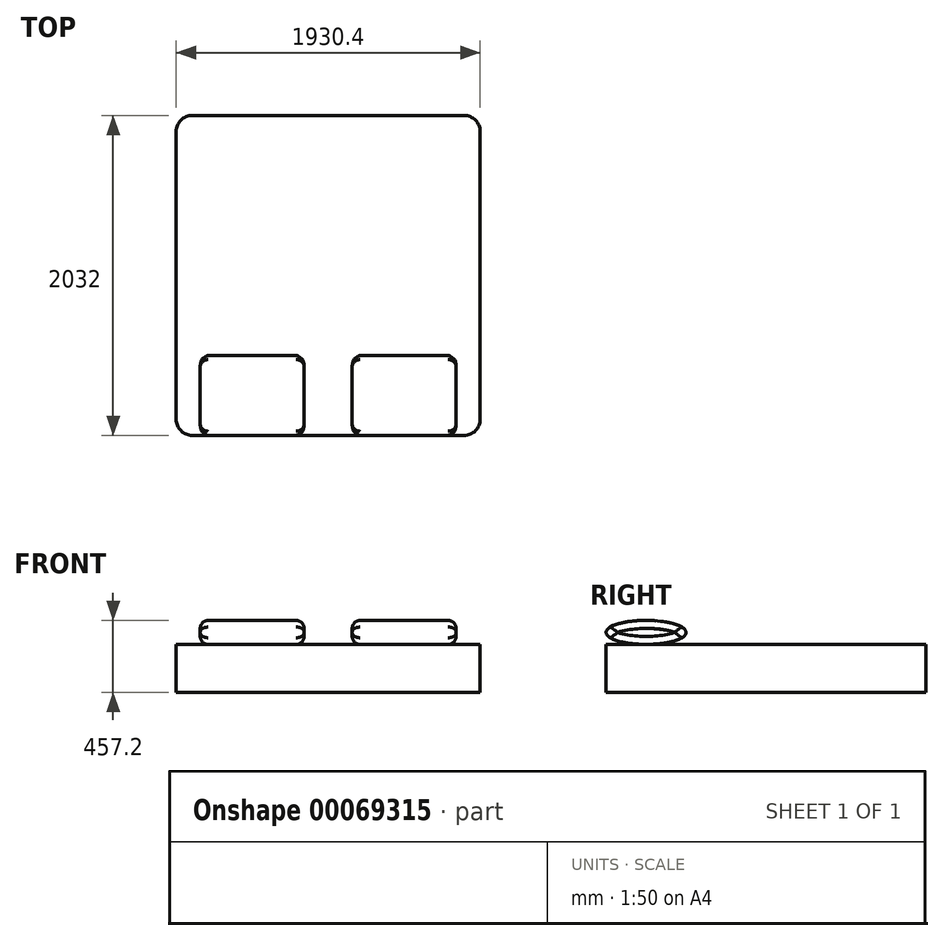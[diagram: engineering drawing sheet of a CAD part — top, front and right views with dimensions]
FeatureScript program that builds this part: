
annotation { "Feature Type Name" : "Feature", "Feature Type Description" : "" }
export const myFeature = defineFeature(function(context is Context, id is Id, definition is map)
    precondition{}
    {
        {
            var Q0;
            Q0=qCreatedBy(makeId("Top.planeOp"),FACE);
            var sketch = newSketch(context, id + "F0", { "sketchPlane" : qUnion([Q0])});
            skLineSegment(sketch, "E0.rect.bottom", {"start": v(-965.2, -1016) * mm, "end": v(965.2, -1016) * mm});
            skLineSegment(sketch, "E0.rect.top", {"start": v(-965.2, 1016) * mm, "end": v(965.2, 1016) * mm});
            skLineSegment(sketch, "E0.rect.left", {"start": v(-965.2, -1016) * mm, "end": v(-965.2, 1016) * mm});
            skLineSegment(sketch, "E0.rect.right", {"start": v(965.2, -1016) * mm, "end": v(965.2, 1016) * mm});
            skPoint(sketch, "E0.rect.middle", {"position": v(0, 0) * mm});
            skSolve(sketch);
        }
        {
            var Q0;
            Q0 = qSketchRegion(id + "F0", true);
            extrude(context, id + "F1", {"entities" : qUnion([Q0]), "depth" : 304.8 * mm});
        }
        {
            var Q0;
            Q0=makeQuery(id+"F1.opExtrude","SWEPT_EDGE",EDGE,{"disambiguationData":[OSD([sQuery(id+"F0.wireOp",EDGE,"E0.rect.top"),sQuery(id+"F0.wireOp",EDGE,"E0.rect.left")])]});
            var Q1;
            Q1=makeQuery(id+"F1.opExtrude","SWEPT_EDGE",EDGE,{"disambiguationData":[OSD([sQuery(id+"F0.wireOp",EDGE,"E0.rect.top"),sQuery(id+"F0.wireOp",EDGE,"E0.rect.right")])]});
            var Q2;
            Q2=makeQuery(id+"F1.opExtrude","SWEPT_EDGE",EDGE,{"disambiguationData":[OSD([sQuery(id+"F0.wireOp",EDGE,"E0.rect.bottom"),sQuery(id+"F0.wireOp",EDGE,"E0.rect.left")])]});
            var Q3;
            Q3=makeQuery(id+"F1.opExtrude","SWEPT_EDGE",EDGE,{"disambiguationData":[OSD([sQuery(id+"F0.wireOp",EDGE,"E0.rect.bottom"),sQuery(id+"F0.wireOp",EDGE,"E0.rect.right")])]});
            fillet(context, id + "F2", {"entities" : qUnion([Q0, Q1, Q2, Q3]), "radius" : 101.6 * mm, "tangentPropagation" : true, "allowEdgeOverflow" : false});
        }
        {
            var Q0;
            Q0=qCreatedBy(makeId("Right.planeOp"),FACE);
            cPlane(context, id + "F3", {"entities" : qUnion([Q0]), "cplaneType" : CPlaneType.OFFSET, "offset" : 482.6 * mm, "width" : 152.4 * mm, "height" : 152.4 * mm});
        }
        {
            var Q0;
            Q0=qCreatedBy(id+"F3.planeOp",FACE);
            var sketch = newSketch(context, id + "F4", { "sketchPlane" : qUnion([Q0])});
            skEllipse(sketch, "E1", {"center": v(-762, 381) * mm, "majorRadius": 254 * mm, "minorRadius": 76.2 * mm, "majorAxis": v(1, 0)});
            skLineSegment(sketch, "E2", {"start": v(-762, 457.2) * mm, "end": v(-762, 304.8) * mm, "construction": true});
            skSolve(sketch);
        }
        {
            var Q0;
            Q0 = qSketchRegion(id + "F4", true);
            extrude(context, id + "F5", {"entities" : qUnion([Q0]), "operationType" : NewBodyOperationType.ADD, "endBound" : BoundingType.SYMMETRIC, "depth" : 660.4 * mm});
        }
        {
            var Q0;
            Q0=makeQuery(id+"F5.opExtrude","SWEPT_BODY",BODY,{"disambiguationData":[OSD([sQuery(id+"F4.wireOp",EDGE,"E1")])]});
            var Q1;
            Q1=qCreatedBy(makeId("Right.planeOp"),FACE);
            mirror(context, id + "F6", {"operationType" : NewBodyOperationType.ADD, "entities" : qUnion([Q0]), "mirrorPlane" : qUnion([Q1])});
        }
        {
            var Q0;
            Q0=makeQuery(id+"F6.opPattern","COPY",EDGE,{"derivedFrom":makeQuery(id+"F5.opExtrude","CAP_EDGE",EDGE,{"disambiguationData":[OSD([sQuery(id+"F4.wireOp",EDGE,"E1")])],"isStart":true}),"instanceName":"1"});
            fillet(context, id + "F7", {"entities" : qUnion([Q0]), "radius" : 50.8 * mm, "tangentPropagation" : true, "allowEdgeOverflow" : false});
        }
        {
            var Q0;
            Q0=makeQuery(id+"F6.opPattern","COPY",EDGE,{"derivedFrom":makeQuery(id+"F5.opExtrude","CAP_EDGE",EDGE,{"disambiguationData":[OSD([sQuery(id+"F4.wireOp",EDGE,"E1")])],"isStart":false}),"instanceName":"1"});
            var Q1;
            Q1=makeQuery(id+"F5.opExtrude","CAP_EDGE",EDGE,{"disambiguationData":[OSD([sQuery(id+"F4.wireOp",EDGE,"E1")])],"isStart":true});
            var Q2;
            Q2=makeQuery(id+"F5.opExtrude","CAP_EDGE",EDGE,{"disambiguationData":[OSD([sQuery(id+"F4.wireOp",EDGE,"E1")])],"isStart":false});
            fillet(context, id + "F8", {"entities" : qUnion([Q0, Q1, Q2]), "radius" : 50.8 * mm, "tangentPropagation" : true, "allowEdgeOverflow" : false});
        }
    });
